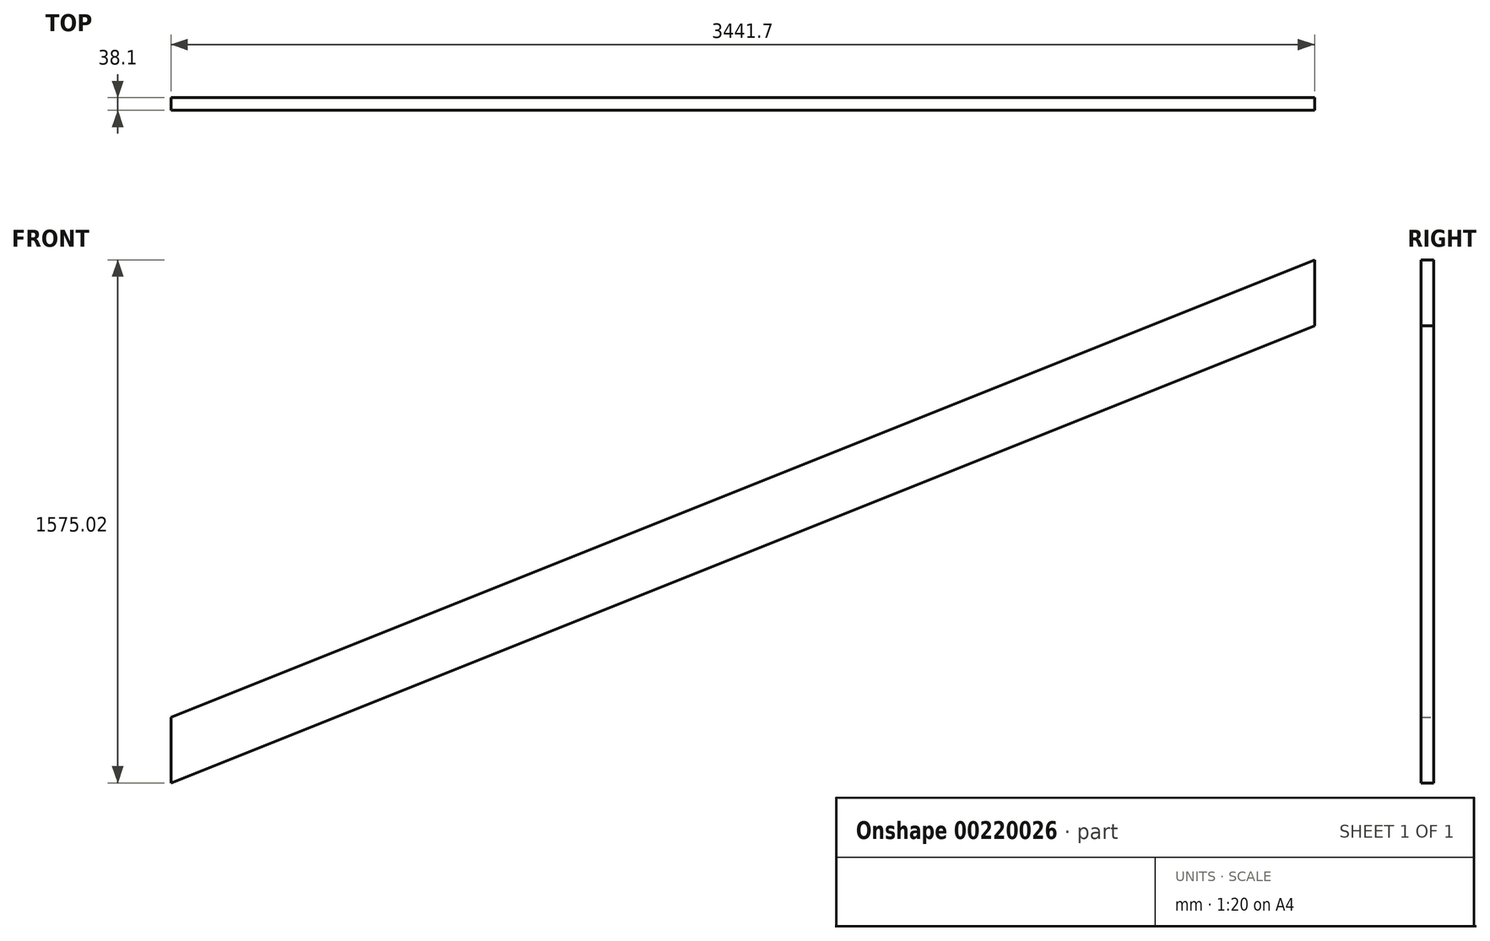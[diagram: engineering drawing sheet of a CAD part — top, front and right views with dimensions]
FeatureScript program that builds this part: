
annotation { "Feature Type Name" : "Feature", "Feature Type Description" : "" }
export const myFeature = defineFeature(function(context is Context, id is Id, definition is map)
    precondition{}
    {
        {
            var Q0;
            Q0=qCreatedBy(makeId("Front.planeOp"),FACE);
            var sketch = newSketch(context, id + "F0", { "sketchPlane" : qUnion([Q0])});
            skLineSegment(sketch, "E0", {"start": v(0, 0) * mm, "end": v(0, 2863.85) * mm, "construction": true});
            skLineSegment(sketch, "E1", {"start": v(0, 2863.85) * mm, "end": v(3048, 4083.05) * mm, "construction": true});
            skLineSegment(sketch, "E2", {"start": v(3048, 4083.05) * mm, "end": v(3048, 0) * mm, "construction": true});
            skLineSegment(sketch, "E3", {"start": v(3048, 0) * mm, "end": v(0, 0) * mm, "construction": true});
            skLineSegment(sketch, "E4", {"start": v(0, 2863.85) * mm, "end": v(-88.9, 2863.85) * mm, "construction": true});
            skLineSegment(sketch, "E5", {"start": v(-88.9, 2863.85) * mm, "end": v(-88.9, 0) * mm, "construction": true});
            skLineSegment(sketch, "E6", {"start": v(-88.9, 0) * mm, "end": v(0, 0) * mm, "construction": true});
            skSolve(sketch);
        }
        {
            var Q0;
            Q0=qCreatedBy(makeId("Front.planeOp"),FACE);
            var sketch = newSketch(context, id + "F1", { "sketchPlane" : qUnion([Q0])});
            skLineSegment(sketch, "E7", {"start": v(3048, 4083.05) * mm, "end": v(-393.7, 2706.37) * mm});
            skLineSegment(sketch, "E8", {"start": v(3048, 4083.05) * mm, "end": v(3048, 4281.39) * mm});
            skLineSegment(sketch, "E9", {"start": v(3048, 4281.39) * mm, "end": v(-393.7, 2904.7) * mm});
            skLineSegment(sketch, "E10", {"start": v(-393.7, 2706.37) * mm, "end": v(-393.7, 2904.7) * mm});
            skSolve(sketch);
        }
        {
            var Q0;
            Q0=makeQuery(id+"F1.imprint","IMPRINT",FACE,{"disambiguationData":[TD([[makeQuery(id+"F1.imprint","IMPRINT",EDGE,{"derivedFrom":sQuery(id+"F1.wireOp",EDGE,"E7")}),-1.0]])]});
            extrude(context, id + "F2", {"entities" : qUnion([Q0]), "depth" : 38.1 * mm});
        }
    });
